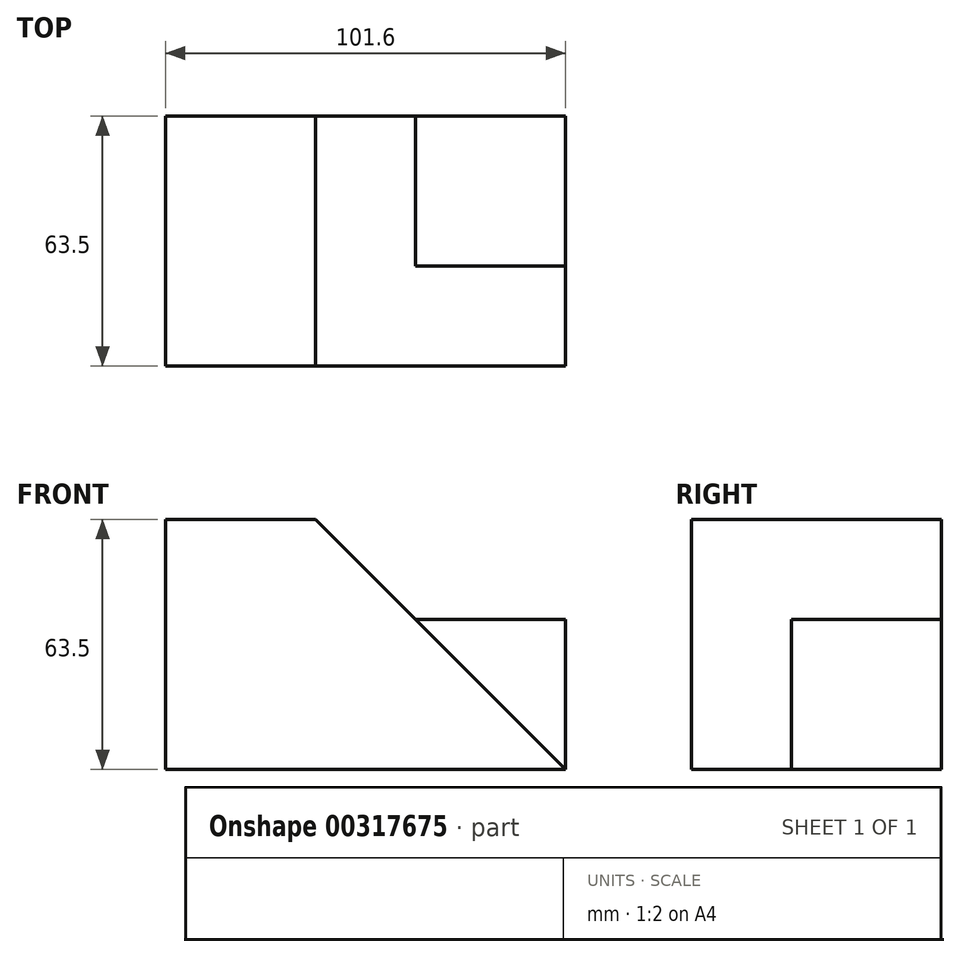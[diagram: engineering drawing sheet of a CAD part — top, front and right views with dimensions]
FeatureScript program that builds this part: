
annotation { "Feature Type Name" : "Feature", "Feature Type Description" : "" }
export const myFeature = defineFeature(function(context is Context, id is Id, definition is map)
    precondition{}
    {
        {
            var Q0;
            Q0=qCreatedBy(makeId("Front.planeOp"),FACE);
            var sketch = newSketch(context, id + "F0", { "sketchPlane" : qUnion([Q0])});
            skLineSegment(sketch, "E0", {"start": v(-63.04, -34.94) * mm, "end": v(38.56, -34.94) * mm});
            skLineSegment(sketch, "E1", {"start": v(-63.04, -34.94) * mm, "end": v(-63.04, 28.56) * mm});
            skLineSegment(sketch, "E2", {"start": v(-63.04, 28.56) * mm, "end": v(-24.94, 28.56) * mm});
            skLineSegment(sketch, "E3", {"start": v(-24.94, 28.56) * mm, "end": v(38.56, -34.94) * mm});
            skSolve(sketch);
        }
        {
            var Q0;
            Q0 = qSketchRegion(id + "F0", true);
            extrude(context, id + "F1", {"entities" : qUnion([Q0]), "depth" : 63.5 * mm});
        }
        {
            var Q0;
            Q0=makeQuery(id+"F1.opExtrude","CAP_FACE",FACE,{"disambiguationData":[OSD([sQuery(id+"F0.wireOp",EDGE,"E0"),sQuery(id+"F0.wireOp",EDGE,"E1"),sQuery(id+"F0.wireOp",EDGE,"E2"),sQuery(id+"F0.wireOp",EDGE,"E3")])],"isStart":true});
            var sketch = newSketch(context, id + "F2", { "sketchPlane" : qUnion([Q0])});
            skLineSegment(sketch, "E4", {"start": v(-38.56, -34.94) * mm, "end": v(-38.56, 3.16) * mm});
            skLineSegment(sketch, "E5", {"start": v(-38.56, 3.16) * mm, "end": v(-0.46, 3.16) * mm});
            skLineSegment(sketch, "E6", {"start": v(-0.46, 3.16) * mm, "end": v(-38.56, -34.94) * mm});
            skLineSegment(sketch, "E7", {"start": v(-38.56, -34.94) * mm, "end": v(-0.46, 3.16) * mm});
            skSolve(sketch);
        }
        {
            var Q0;
            Q0 = qSketchRegion(id + "F2", true);
            extrude(context, id + "F3", {"entities" : qUnion([Q0]), "operationType" : NewBodyOperationType.ADD, "oppositeDirection" : true, "depth" : 25.4 * mm});
        }
        {
            var Q0;
            Q0=makeQuery(id+"F2.imprint","IMPRINT",FACE,{"disambiguationData":[TD([[makeQuery(id+"F2.imprint","IMPRINT",EDGE,{"derivedFrom":sQuery(id+"F2.wireOp",EDGE,"E4")}),-1.0]])]});
            extrude(context, id + "F4", {"entities" : qUnion([Q0]), "operationType" : NewBodyOperationType.ADD, "oppositeDirection" : true, "depth" : 38.1 * mm});
        }
    });
